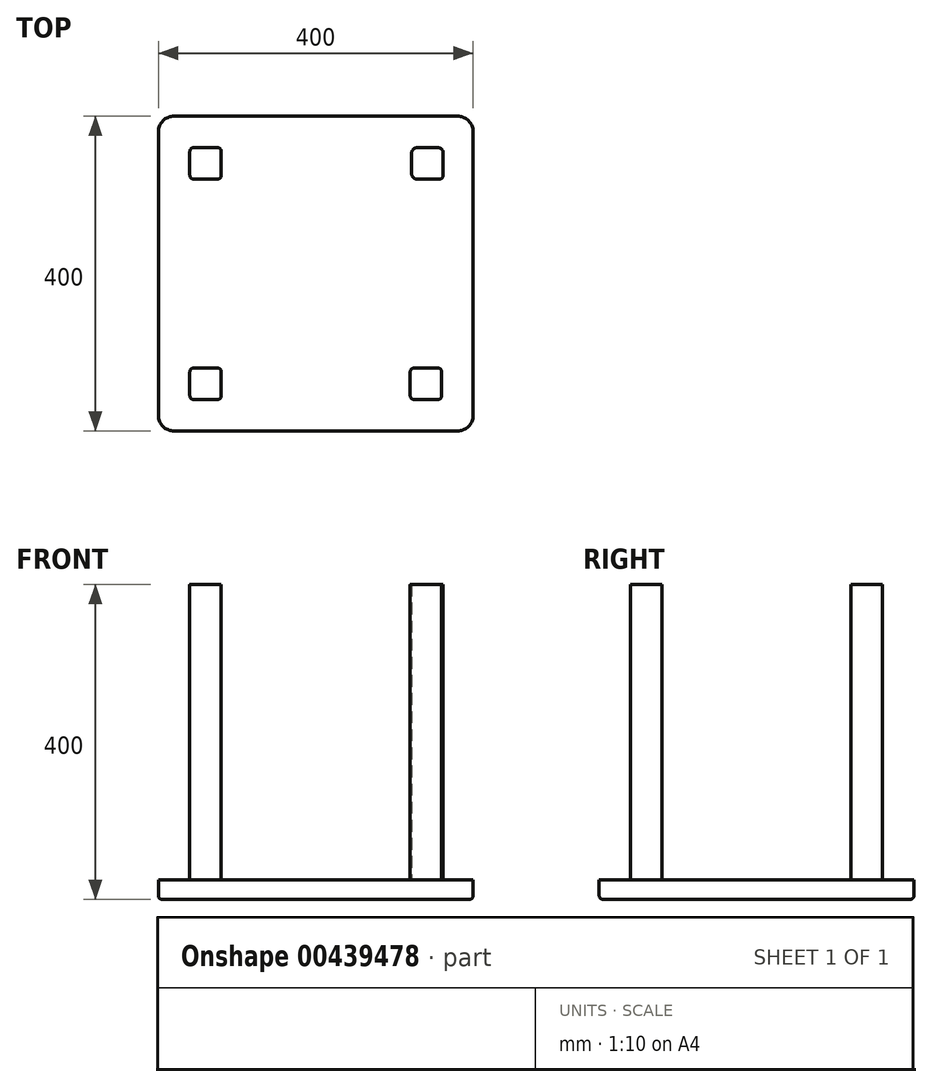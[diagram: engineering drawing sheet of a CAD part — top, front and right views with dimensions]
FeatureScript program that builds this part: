
annotation { "Feature Type Name" : "Feature", "Feature Type Description" : "" }
export const myFeature = defineFeature(function(context is Context, id is Id, definition is map)
    precondition{}
    {
        {
            var Q0;
            Q0=qCreatedBy(makeId("Top.planeOp"),FACE);
            var sketch = newSketch(context, id + "F0", { "sketchPlane" : qUnion([Q0])});
            skLineSegment(sketch, "E0.bottom", {"start": v(-175.65, 213.83) * mm, "end": v(184.35, 213.83) * mm});
            skLineSegment(sketch, "E0.top", {"start": v(-175.65, -186.17) * mm, "end": v(184.35, -186.17) * mm});
            skLineSegment(sketch, "E0.left", {"start": v(-195.65, 193.83) * mm, "end": v(-195.65, -166.17) * mm});
            skLineSegment(sketch, "E0.right", {"start": v(204.35, 193.83) * mm, "end": v(204.35, -166.17) * mm});
            skPoint(sketch, "E1.visualSharp", {"position": v(-195.65, 213.83) * mm});
            skArc(sketch, "E1.filletArc", {"start": v(-175.65, 213.83) * mm, "mid": v(-189.79, 207.97) * mm, "end": v(-195.65, 193.83) * mm});
            skPoint(sketch, "E2.visualSharp", {"position": v(204.35, 213.83) * mm});
            skArc(sketch, "E2.filletArc", {"start": v(204.35, 193.83) * mm, "mid": v(198.5, 207.97) * mm, "end": v(184.35, 213.83) * mm});
            skPoint(sketch, "E3.visualSharp", {"position": v(204.35, -186.17) * mm});
            skArc(sketch, "E3.filletArc", {"start": v(184.35, -186.17) * mm, "mid": v(198.5, -180.31) * mm, "end": v(204.35, -166.17) * mm});
            skPoint(sketch, "E4.visualSharp", {"position": v(-195.65, -186.17) * mm});
            skArc(sketch, "E4.filletArc", {"start": v(-195.65, -166.17) * mm, "mid": v(-189.79, -180.31) * mm, "end": v(-175.65, -186.17) * mm});
            skSolve(sketch);
        }
        {
            var Q0;
            Q0=makeQuery(id+"F0.imprint","IMPRINT",FACE,{"disambiguationData":[TD([[makeQuery(id+"F0.imprint","IMPRINT",EDGE,{"derivedFrom":sQuery(id+"F0.wireOp",EDGE,"E0.bottom")}),-1.0]])]});
            extrude(context, id + "F1", {"entities" : qUnion([Q0]), "depth" : 25 * mm});
        }
        {
            var Q0;
            Q0=makeQuery(id+"F1.opExtrude","CAP_FACE",FACE,{"disambiguationData":[OSD([sQuery(id+"F0.wireOp",EDGE,"E0.bottom"),sQuery(id+"F0.wireOp",EDGE,"E0.top"),sQuery(id+"F0.wireOp",EDGE,"E0.left"),sQuery(id+"F0.wireOp",EDGE,"E0.right"),sQuery(id+"F0.wireOp",EDGE,"E1.filletArc"),sQuery(id+"F0.wireOp",EDGE,"E2.filletArc"),sQuery(id+"F0.wireOp",EDGE,"E3.filletArc"),sQuery(id+"F0.wireOp",EDGE,"E4.filletArc")])],"isStart":false});
            var sketch = newSketch(context, id + "F2", { "sketchPlane" : qUnion([Q0])});
            skLineSegment(sketch, "E5.bottom", {"start": v(-150.65, 173.83) * mm, "end": v(-120.65, 173.83) * mm});
            skLineSegment(sketch, "E5.top", {"start": v(-150.65, 133.83) * mm, "end": v(-120.65, 133.83) * mm});
            skLineSegment(sketch, "E5.left", {"start": v(-155.65, 168.83) * mm, "end": v(-155.65, 138.83) * mm});
            skLineSegment(sketch, "E5.right", {"start": v(-115.65, 168.83) * mm, "end": v(-115.65, 138.83) * mm});
            skPoint(sketch, "E6.visualSharp", {"position": v(-155.65, 133.83) * mm});
            skArc(sketch, "E6.filletArc", {"start": v(-155.65, 138.83) * mm, "mid": v(-154.18, 135.3) * mm, "end": v(-150.65, 133.83) * mm});
            skPoint(sketch, "E7.visualSharp", {"position": v(-115.65, 133.83) * mm});
            skArc(sketch, "E7.filletArc", {"start": v(-120.65, 133.83) * mm, "mid": v(-117.11, 135.3) * mm, "end": v(-115.65, 138.83) * mm});
            skPoint(sketch, "E8.visualSharp", {"position": v(-115.65, 173.83) * mm});
            skArc(sketch, "E8.filletArc", {"start": v(-115.65, 168.83) * mm, "mid": v(-117.11, 172.36) * mm, "end": v(-120.65, 173.83) * mm});
            skPoint(sketch, "E9.visualSharp", {"position": v(-155.65, 173.83) * mm});
            skArc(sketch, "E9.filletArc", {"start": v(-150.65, 173.83) * mm, "mid": v(-154.18, 172.36) * mm, "end": v(-155.65, 168.83) * mm});
            skSolve(sketch);
        }
        {
            var Q0;
            Q0=makeQuery(id+"F2.imprint","IMPRINT",FACE,{"disambiguationData":[TD([[makeQuery(id+"F2.imprint","IMPRINT",EDGE,{"derivedFrom":sQuery(id+"F2.wireOp",EDGE,"E5.bottom")}),1.0]])]});
            var sketch = newSketch(context, id + "F3", { "sketchPlane" : qUnion([Q0])});
            skLineSegment(sketch, "E10.bottom", {"start": v(-150.65, -106.17) * mm, "end": v(-120.65, -106.17) * mm});
            skLineSegment(sketch, "E10.top", {"start": v(-150.65, -146.17) * mm, "end": v(-120.65, -146.17) * mm});
            skLineSegment(sketch, "E10.left", {"start": v(-155.65, -111.17) * mm, "end": v(-155.65, -141.17) * mm});
            skLineSegment(sketch, "E10.right", {"start": v(-115.65, -111.17) * mm, "end": v(-115.65, -141.17) * mm});
            skPoint(sketch, "E11.visualSharp", {"position": v(-155.65, -146.17) * mm});
            skArc(sketch, "E11.filletArc", {"start": v(-155.65, -141.17) * mm, "mid": v(-154.18, -144.7) * mm, "end": v(-150.65, -146.17) * mm});
            skPoint(sketch, "E12.visualSharp", {"position": v(-115.65, -146.17) * mm});
            skArc(sketch, "E12.filletArc", {"start": v(-120.65, -146.17) * mm, "mid": v(-117.11, -144.7) * mm, "end": v(-115.65, -141.17) * mm});
            skPoint(sketch, "E13.visualSharp", {"position": v(-115.65, -106.17) * mm});
            skArc(sketch, "E13.filletArc", {"start": v(-115.65, -111.17) * mm, "mid": v(-117.11, -107.64) * mm, "end": v(-120.65, -106.17) * mm});
            skPoint(sketch, "E14.visualSharp", {"position": v(-155.65, -106.17) * mm});
            skArc(sketch, "E14.filletArc", {"start": v(-150.65, -106.17) * mm, "mid": v(-154.18, -107.64) * mm, "end": v(-155.65, -111.17) * mm});
            skSolve(sketch);
        }
        {
            var Q0;
            Q0=makeQuery(id+"F2.imprint","IMPRINT",FACE,{"disambiguationData":[TD([[makeQuery(id+"F2.imprint","IMPRINT",EDGE,{"derivedFrom":sQuery(id+"F2.wireOp",EDGE,"E5.bottom")}),1.0]])]});
            var sketch = newSketch(context, id + "F4", { "sketchPlane" : qUnion([Q0])});
            skLineSegment(sketch, "E15.bottom", {"start": v(132.94, 173.83) * mm, "end": v(159.64, 173.83) * mm});
            skLineSegment(sketch, "E15.top", {"start": v(132.94, 133.83) * mm, "end": v(161.29, 133.83) * mm});
            skLineSegment(sketch, "E15.left", {"start": v(126.29, 167.18) * mm, "end": v(126.29, 140.48) * mm});
            skLineSegment(sketch, "E15.right", {"start": v(166.29, 167.18) * mm, "end": v(166.29, 138.83) * mm});
            skPoint(sketch, "E16.visualSharp", {"position": v(126.29, 133.83) * mm});
            skArc(sketch, "E16.filletArc", {"start": v(126.29, 140.48) * mm, "mid": v(128.23, 135.78) * mm, "end": v(132.94, 133.83) * mm});
            skPoint(sketch, "E17.visualSharp", {"position": v(166.29, 133.83) * mm});
            skArc(sketch, "E17.filletArc", {"start": v(161.29, 133.83) * mm, "mid": v(164.82, 135.3) * mm, "end": v(166.29, 138.83) * mm});
            skPoint(sketch, "E18.visualSharp", {"position": v(166.29, 173.83) * mm});
            skArc(sketch, "E18.filletArc", {"start": v(166.29, 167.18) * mm, "mid": v(164.34, 171.88) * mm, "end": v(159.64, 173.83) * mm});
            skPoint(sketch, "E19.visualSharp", {"position": v(126.29, 173.83) * mm});
            skArc(sketch, "E19.filletArc", {"start": v(132.94, 173.83) * mm, "mid": v(128.23, 171.88) * mm, "end": v(126.29, 167.18) * mm});
            skSolve(sketch);
        }
        {
            var Q0;
            Q0=makeQuery(id+"F2.imprint","IMPRINT",FACE,{"disambiguationData":[TD([[makeQuery(id+"F2.imprint","IMPRINT",EDGE,{"derivedFrom":sQuery(id+"F2.wireOp",EDGE,"E5.bottom")}),1.0]])]});
            var sketch = newSketch(context, id + "F5", { "sketchPlane" : qUnion([Q0])});
            skLineSegment(sketch, "E20.bottom", {"start": v(129.35, -106.17) * mm, "end": v(159.35, -106.17) * mm});
            skLineSegment(sketch, "E20.top", {"start": v(129.35, -146.17) * mm, "end": v(159.35, -146.17) * mm});
            skLineSegment(sketch, "E20.left", {"start": v(124.35, -111.17) * mm, "end": v(124.35, -141.17) * mm});
            skLineSegment(sketch, "E20.right", {"start": v(164.35, -111.17) * mm, "end": v(164.35, -141.17) * mm});
            skPoint(sketch, "E21.visualSharp", {"position": v(124.35, -146.17) * mm});
            skArc(sketch, "E21.filletArc", {"start": v(124.35, -141.17) * mm, "mid": v(125.82, -144.7) * mm, "end": v(129.35, -146.17) * mm});
            skPoint(sketch, "E22.visualSharp", {"position": v(164.35, -146.17) * mm});
            skArc(sketch, "E22.filletArc", {"start": v(159.35, -146.17) * mm, "mid": v(162.89, -144.7) * mm, "end": v(164.35, -141.17) * mm});
            skPoint(sketch, "E23.visualSharp", {"position": v(164.35, -106.17) * mm});
            skArc(sketch, "E23.filletArc", {"start": v(164.35, -111.17) * mm, "mid": v(162.89, -107.64) * mm, "end": v(159.35, -106.17) * mm});
            skPoint(sketch, "E24.visualSharp", {"position": v(124.35, -106.17) * mm});
            skArc(sketch, "E24.filletArc", {"start": v(129.35, -106.17) * mm, "mid": v(125.82, -107.64) * mm, "end": v(124.35, -111.17) * mm});
            skSolve(sketch);
        }
        {
            var Q0;
            Q0 = qSketchRegion(id + "F2", true);
            var Q1;
            Q1 = qSketchRegion(id + "F3", true);
            var Q2;
            Q2 = qSketchRegion(id + "F4", true);
            var Q3;
            Q3 = qSketchRegion(id + "F5", true);
            extrude(context, id + "F6", {"entities" : qUnion([Q0, Q1, Q2, Q3]), "operationType" : NewBodyOperationType.ADD, "depth" : 375 * mm});
        }
        {
            var Q0;
            Q0=makeQuery(id+"F1.opExtrude","CAP_EDGE",EDGE,{"disambiguationData":[OSD([sQuery(id+"F0.wireOp",EDGE,"E0.top")])],"isStart":true});
            fillet(context, id + "F7", {"entities" : qUnion([Q0]), "radius" : 5 * mm, "tangentPropagation" : true, "allowEdgeOverflow" : false});
        }
    });
